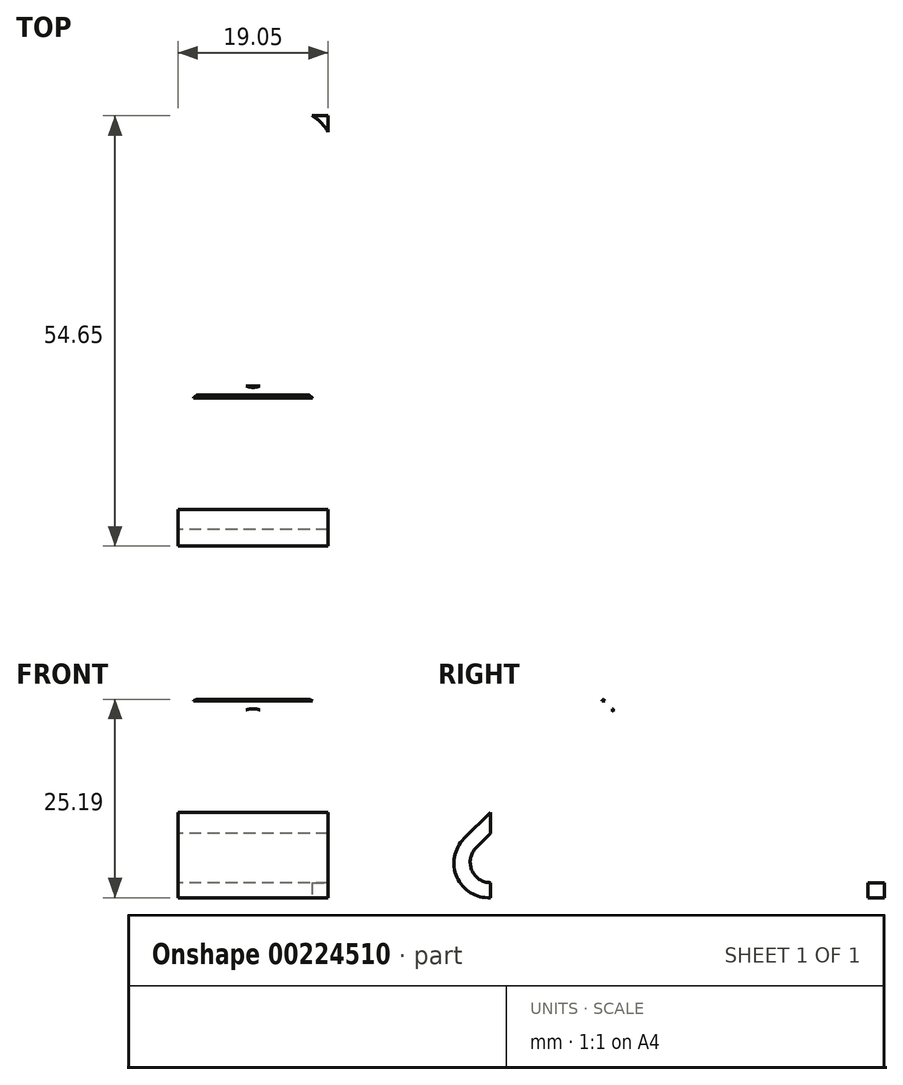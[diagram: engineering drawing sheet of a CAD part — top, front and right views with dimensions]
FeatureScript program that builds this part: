
annotation { "Feature Type Name" : "Feature", "Feature Type Description" : "" }
export const myFeature = defineFeature(function(context is Context, id is Id, definition is map)
    precondition{}
    {
        {
            var Q0;
            Q0=qCreatedBy(makeId("Right.planeOp"),FACE);
            var sketch = newSketch(context, id + "F0", { "sketchPlane" : qUnion([Q0])});
            skLineSegment(sketch, "E0", {"start": v(25, 1.9) * mm, "end": v(-25, 1.9) * mm});
            skArc(sketch, "E1", {"start": v(-28.36, 7.5) * mm, "mid": v(-29.26, 2.6) * mm, "end": v(-25, 0) * mm});
            skLineSegment(sketch, "E2", {"start": v(-28.36, 7.5) * mm, "end": v(-10.68, 25.18) * mm});
            skLineSegment(sketch, "E3", {"start": v(-10.68, 25.18) * mm, "end": v(-9.34, 23.84) * mm});
            skLineSegment(sketch, "E4", {"start": v(-9.34, 23.84) * mm, "end": v(-26.82, 6.35) * mm});
            skArc(sketch, "E5", {"start": v(-26.82, 6.35) * mm, "mid": v(-27.4, 3.52) * mm, "end": v(-25, 1.9) * mm});
            skLineSegment(sketch, "E6", {"start": v(-25, 0) * mm, "end": v(25, 0) * mm});
            skLineSegment(sketch, "E7", {"start": v(25, 0) * mm, "end": v(25, 1.9) * mm});
            skSolve(sketch);
        }
        {
            var Q0;
            Q0=makeQuery(id+"F0.imprint","IMPRINT",FACE,{"disambiguationData":[TD([[makeQuery(id+"F0.imprint","IMPRINT",EDGE,{"derivedFrom":sQuery(id+"F0.wireOp",EDGE,"E0")}),1.0]])]});
            extrude(context, id + "F1", {"entities" : qUnion([Q0]), "depth" : 19.05 * mm});
        }
        {
            var Q0;
            Q0=makeQuery(id+"F1.opExtrude","SWEPT_FACE",FACE,{"disambiguationData":[OSD([sQuery(id+"F0.wireOp",EDGE,"E6")])]});
            var sketch = newSketch(context, id + "F2", { "sketchPlane" : qUnion([Q0])});
            skArc(sketch, "E8", {"start": v(7.03, -20.5) * mm, "mid": v(9.53, -23) * mm, "end": v(12.03, -20.5) * mm});
            skLineSegment(sketch, "E9", {"start": v(7.03, -20.5) * mm, "end": v(7.03, -5.5) * mm});
            skLineSegment(sketch, "E10", {"start": v(12.03, -20.5) * mm, "end": v(12.03, -5.5) * mm});
            skArc(sketch, "E11", {"start": v(12.02, -5.5) * mm, "mid": v(9.53, -3) * mm, "end": v(7.03, -5.5) * mm});
            skPoint(sketch, "E12.endSnap0", {"position": v(9.53, -3) * mm});
            skCircle(sketch, "E13", {"center": v(9.53, 7) * mm, "radius": 2.5 * mm});
            skSolve(sketch);
        }
        {
            var Q0;
            Q0=makeQuery(id+"F2.imprint","IMPRINT",FACE,{"disambiguationData":[TD([[makeQuery(id+"F2.imprint","IMPRINT",EDGE,{"derivedFrom":sQuery(id+"F2.wireOp",EDGE,"E8")}),1.0]])]});
            var Q1;
            Q1=makeQuery(id+"F2.imprint","IMPRINT",FACE,{"disambiguationData":[TD([[makeQuery(id+"F2.imprint","IMPRINT",EDGE,{"derivedFrom":sQuery(id+"F2.wireOp",EDGE,"E13")}),1.0]])]});
            extrude(context, id + "F3", {"entities" : qUnion([Q0, Q1]), "operationType" : NewBodyOperationType.REMOVE, "oppositeDirection" : true, "depth" : 22 * mm});
        }
        {
            var Q0;
            Q0=makeQuery(id+"F1.opExtrude","SWEPT_FACE",FACE,{"disambiguationData":[OSD([sQuery(id+"F0.wireOp",EDGE,"E6")])]});
            var sketch = newSketch(context, id + "F4", { "sketchPlane" : qUnion([Q0])});
            skArc(sketch, "E14", {"start": v(0, -22.92) * mm, "mid": v(0.86, -24.1) * mm, "end": v(2.02, -25) * mm});
            skArc(sketch, "E15.MirrorCS", {"start": v(19.05, -22.92) * mm, "mid": v(18.2, -24.1) * mm, "end": v(17.03, -25) * mm});
            skLineSegment(sketch, "E16", {"start": v(0, -22.92) * mm, "end": v(0, -25) * mm});
            skLineSegment(sketch, "E17", {"start": v(0, -25) * mm, "end": v(2.02, -25) * mm});
            skLineSegment(sketch, "E18", {"start": v(19.05, -25) * mm, "end": v(19.05, -22.92) * mm});
            skLineSegment(sketch, "E19", {"start": v(17.03, -25) * mm, "end": v(19.05, -25) * mm});
            skSolve(sketch);
        }
        {
            var Q0;
            Q0=makeQuery(id+"F4.imprint","IMPRINT",FACE,{"disambiguationData":[TD([[makeQuery(id+"F4.imprint","IMPRINT",EDGE,{"derivedFrom":sQuery(id+"F4.wireOp",EDGE,"E14")}),-1.0]])]});
            var Q1;
            Q1=makeQuery(id+"F4.imprint","IMPRINT",FACE,{"disambiguationData":[TD([[makeQuery(id+"F4.imprint","IMPRINT",EDGE,{"derivedFrom":sQuery(id+"F4.wireOp",EDGE,"E15.MirrorCS")}),1.0]])]});
            extrude(context, id + "F5", {"entities" : qUnion([Q0, Q1]), "operationType" : NewBodyOperationType.REMOVE, "oppositeDirection" : true, "depth" : 25 * mm});
        }
        {
            var Q0;
            Q0=makeQuery(id+"F1.opExtrude","SWEPT_FACE",FACE,{"disambiguationData":[OSD([sQuery(id+"F0.wireOp",EDGE,"E2")])]});
            var sketch = newSketch(context, id + "F6", { "sketchPlane" : qUnion([Q0])});
            skArc(sketch, "E20", {"start": v(2.36, 10.25) * mm, "mid": v(0.9, 9.02) * mm, "end": v(0, 7.32) * mm});
            skLineSegment(sketch, "E21", {"start": v(0, 7.32) * mm, "end": v(0, 10.25) * mm});
            skLineSegment(sketch, "E22", {"start": v(0, 10.25) * mm, "end": v(2.36, 10.25) * mm});
            skPoint(sketch, "E23.endSnap0", {"position": v(9.53, 10.25) * mm});
            skLineSegment(sketch, "E24", {"start": v(19.05, 7.32) * mm, "end": v(19.05, 10.25) * mm});
            skLineSegment(sketch, "E25", {"start": v(19.05, 10.25) * mm, "end": v(16.69, 10.25) * mm});
            skArc(sketch, "E26.MirrorCS", {"start": v(16.69, 10.25) * mm, "mid": v(18.16, 9.02) * mm, "end": v(19.05, 7.32) * mm});
            skSolve(sketch);
        }
        {
            var Q0;
            Q0=makeQuery(id+"F6.imprint","IMPRINT",FACE,{"disambiguationData":[TD([[makeQuery(id+"F6.imprint","IMPRINT",EDGE,{"derivedFrom":sQuery(id+"F6.wireOp",EDGE,"E20")}),-1.0]])]});
            var Q1;
            Q1=makeQuery(id+"F6.imprint","IMPRINT",FACE,{"disambiguationData":[TD([[makeQuery(id+"F6.imprint","IMPRINT",EDGE,{"derivedFrom":sQuery(id+"F6.wireOp",EDGE,"E25")}),1.0]])]});
            extrude(context, id + "F7", {"entities" : qUnion([Q0, Q1]), "operationType" : NewBodyOperationType.REMOVE, "oppositeDirection" : true, "depth" : 5 * mm});
        }
        {
            var Q0;
            Q0=makeQuery(id+"F1.opExtrude","SWEPT_FACE",FACE,{"disambiguationData":[OSD([sQuery(id+"F0.wireOp",EDGE,"E2")])]});
            var sketch = newSketch(context, id + "F8", { "sketchPlane" : qUnion([Q0])});
            skCircle(sketch, "E27", {"center": v(4.5, 2.75) * mm, "radius": 1.86 * mm});
            skLineSegment(sketch, "E28", {"start": v(9.53, 10.25) * mm, "end": v(9.53, 0) * mm, "construction": true});
            skCircle(sketch, "E29.MirrorC", {"center": v(14.55, 2.75) * mm, "radius": 1.86 * mm});
            skSolve(sketch);
        }
        {
            var Q0;
            Q0=makeQuery(id+"F8.imprint","IMPRINT",FACE,{"disambiguationData":[TD([[makeQuery(id+"F8.imprint","IMPRINT",EDGE,{"derivedFrom":sQuery(id+"F8.wireOp",EDGE,"E27")}),1.0]])]});
            var Q1;
            Q1=makeQuery(id+"F8.imprint","IMPRINT",FACE,{"disambiguationData":[TD([[makeQuery(id+"F8.imprint","IMPRINT",EDGE,{"derivedFrom":sQuery(id+"F8.wireOp",EDGE,"E29.MirrorC")}),-1.0]])]});
            extrude(context, id + "F9", {"entities" : qUnion([Q0, Q1]), "operationType" : NewBodyOperationType.REMOVE, "oppositeDirection" : true, "depth" : 5 * mm});
        }
    });
